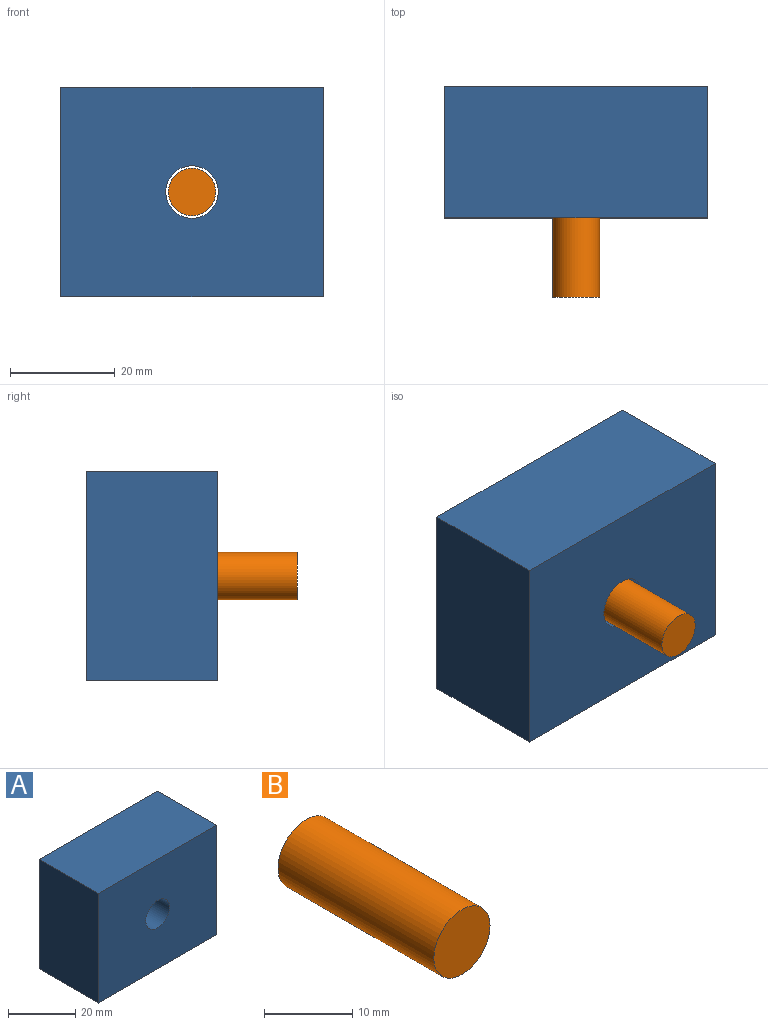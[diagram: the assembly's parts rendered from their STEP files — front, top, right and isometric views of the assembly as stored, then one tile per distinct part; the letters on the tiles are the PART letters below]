
ASSEMBLY  parts=2 mates=1
PART A: 7 faces, bbox 50x25x40 mm
  f0: plane 40x25mm, normal (-1,0,0), area 1000mm2, adj f1,f3,f5,f6
  f1: plane 50x25mm, normal (0,0,-1), area 1250mm2, adj f0,f2,f5,f6
  f2: plane 40x25mm, normal (1,0,0), area 1000mm2, adj f1,f3,f5,f6
  f3: plane 50x25mm, normal (0,0,1), area 1250mm2, adj f0,f2,f5,f6
  f4: cylinder r=5mm len=25mm, axis (0,1,0), area 785.4mm2, adj f5,f6
  f5: plane 50x40mm, normal (0,-1,0), area 1921.5mm2, adj f0,f1,f2,f3,f4
  f6: plane 50x40mm, normal (0,1,0), area 1921.5mm2, adj f0,f1,f2,f3,f4
PART B: 3 faces, bbox 9x25x9 mm
  f0: cylinder r=4.5mm len=25mm, axis (0,-1,0), area 706.9mm2, adj f1,f2
  f1: plane 9x9mm, normal (0,1,0), area 63.6mm2, adj f0
  f2: plane 9x9mm, normal (0,-1,0), area 63.6mm2, adj f0
PLACE A t=(-2.01,0,-2.23)mm
PLACE B t=(-2.53,9.85,-3.29)mm
MATE cylindrical B.f0 <-> A.f4  axis (0,-1,0) through (22.99,-27.65,17.77)mm
